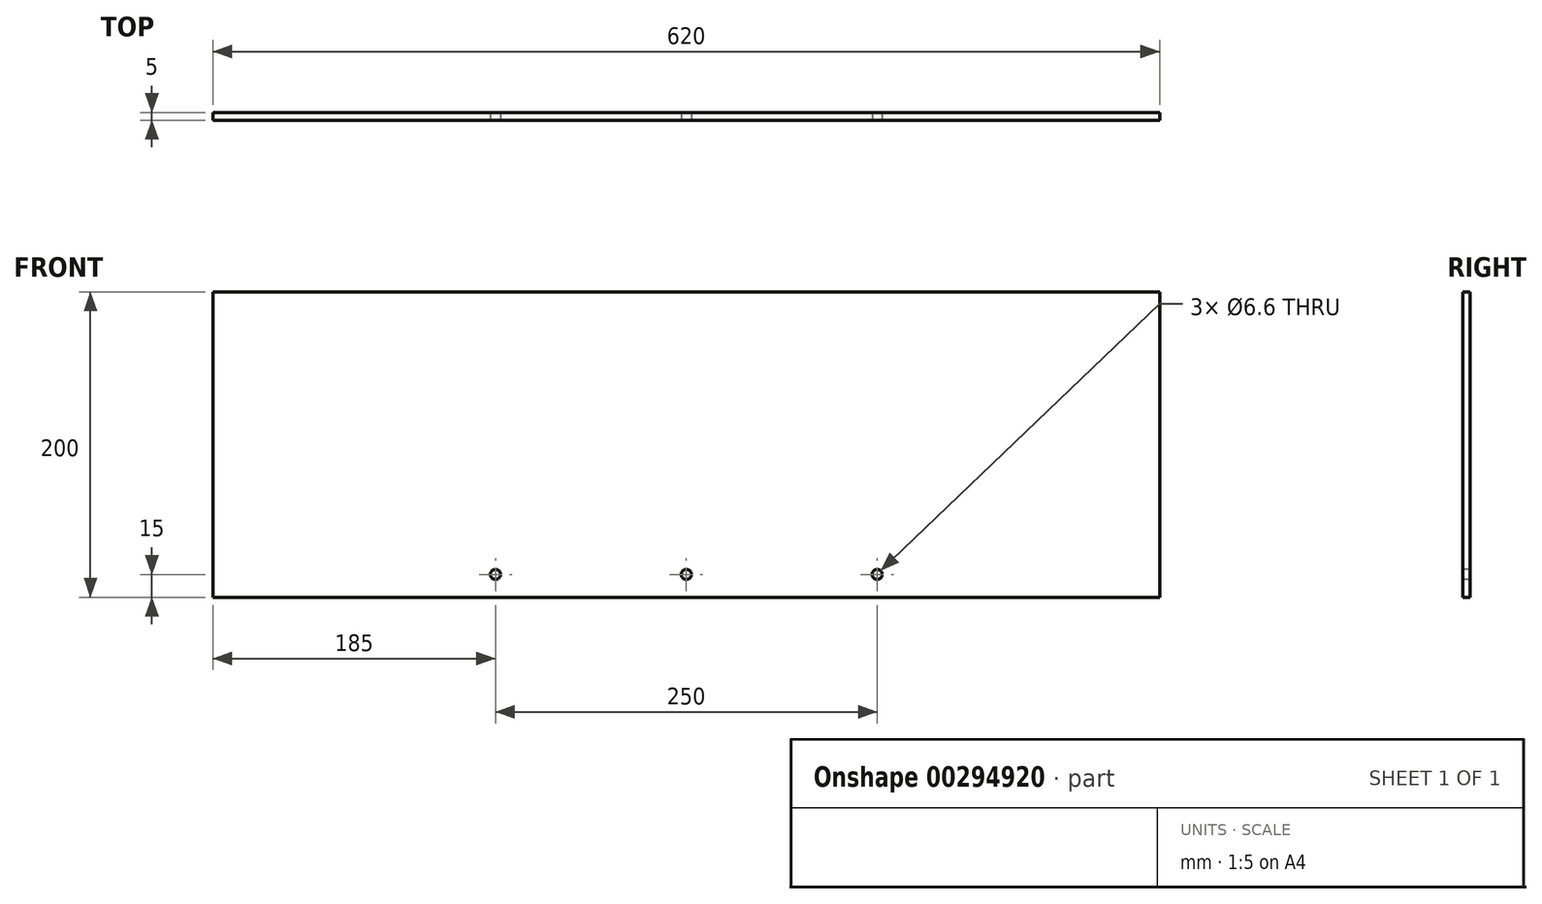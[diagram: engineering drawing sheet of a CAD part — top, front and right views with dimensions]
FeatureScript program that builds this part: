
annotation { "Feature Type Name" : "Feature", "Feature Type Description" : "" }
export const myFeature = defineFeature(function(context is Context, id is Id, definition is map)
    precondition{}
    {
        {
            var Q0;
            Q0=qCreatedBy(makeId("Front.planeOp"),FACE);
            var sketch = newSketch(context, id + "F0", { "sketchPlane" : qUnion([Q0])});
            skLineSegment(sketch, "E0.bottom", {"start": v(-310, 100) * mm, "end": v(310, 100) * mm});
            skLineSegment(sketch, "E0.top", {"start": v(-310, -100) * mm, "end": v(310, -100) * mm});
            skLineSegment(sketch, "E0.left", {"start": v(-310, 100) * mm, "end": v(-310, -100) * mm});
            skLineSegment(sketch, "E0.right", {"start": v(310, 100) * mm, "end": v(310, -100) * mm});
            skPoint(sketch, "E0.middle", {"position": v(0, 0) * mm});
            skLineSegment(sketch, "E1", {"start": v(-250, 100) * mm, "end": v(-250, -100) * mm, "construction": true});
            skLineSegment(sketch, "E2", {"start": v(-310, 100) * mm, "end": v(310, 100) * mm, "construction": true});
            skLineSegment(sketch, "E3", {"start": v(-250, 100) * mm, "end": v(310, 100) * mm});
            skSolve(sketch);
        }
        {
            var Q0;
            {var subQ1=sQuery(id+"F0.wireOp",EDGE,"E0.top");Q0=makeQuery(id+"F0.imprint","IMPRINT",FACE,{"disambiguationData":[TD([[makeQuery(id+"F0.imprint","IMPRINT",EDGE,{"derivedFrom":subQ1}),1.0]])]});}
            extrude(context, id + "F1", {"entities" : qUnion([Q0]), "depth" : 5 * mm, "offsetDistance" : 25 * mm});
        }
        {
            var Q0;
            Q0=makeQuery(id+"F1.opExtrude","CAP_FACE",FACE,{"disambiguationData":[OSD([sQuery(id+"F0.wireOp",EDGE,"E0.bottom"),sQuery(id+"F0.wireOp",EDGE,"E0.top"),sQuery(id+"F0.wireOp",EDGE,"E0.left"),sQuery(id+"F0.wireOp",EDGE,"E0.right"),sQuery(id+"F0.wireOp",EDGE,"E3")])],"isStart":false});
            var sketch = newSketch(context, id + "F2", { "sketchPlane" : qUnion([Q0])});
            skLineSegment(sketch, "E4", {"start": v(-310, -85) * mm, "end": v(310, -85) * mm, "construction": true});
            skPoint(sketch, "E5", {"position": v(-125, -85) * mm});
            skPoint(sketch, "E6", {"position": v(125, -85) * mm});
            skPoint(sketch, "E7", {"position": v(0, -85) * mm});
            skLineSegment(sketch, "E8", {"start": v(-250, 100) * mm, "end": v(-250, -100) * mm, "construction": true});
            skSolve(sketch);
        }
        {
            var Q0;
            Q0=sQuery(id+"F2.wireOp",VERTEX,"E5");
            var Q1;
            Q1=sQuery(id+"F2.wireOp",VERTEX,"29e96742-76e6-4ba6-ab32-156a816730d5");
            var Q2;
            Q2=sQuery(id+"F2.wireOp",VERTEX,"E6");
            var Q3;
            Q3=sQuery(id+"F2.wireOp",VERTEX,"E7");
            var Q4;
            Q4=makeQuery(id+"F1.opExtrude","SWEPT_BODY",BODY,{"disambiguationData":[OSD([sQuery(id+"F0.wireOp",EDGE,"E0.bottom"),sQuery(id+"F0.wireOp",EDGE,"E0.top"),sQuery(id+"F0.wireOp",EDGE,"E0.left"),sQuery(id+"F0.wireOp",EDGE,"E0.right"),sQuery(id+"F0.wireOp",EDGE,"E3")])]});
            hole(context, id + "F3", {"style" : HoleStyle.SIMPLE, "endStyle" : HoleEndStyle.THROUGH, "standardTappedOrClearance" : lookupTablePath({ "standard" : "ISO", "fit" : "Normal", "size" : "M6", "type" : "Clearance" }), "standardBlindInLast" : lookupTablePath({ "fit" : "Standard", "standard" : "ISO", "size" : "M6", "type" : "Clearance" }), "holeDiameter" : 6.6 * mm, "isTappedThrough" : true, "tappedDepth" : 12 * mm, "tapClearance" : 3, "locations" : qUnion([Q0, Q1, Q2, Q3]), "scope" : qUnion([Q4])});
        }
    });
